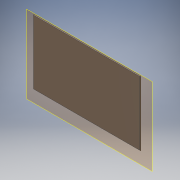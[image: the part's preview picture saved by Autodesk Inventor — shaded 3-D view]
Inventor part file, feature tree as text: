
AUTODESK INVENTOR PART (.ipt)
format: ipt  version: 2016 SP2 (Build 200236200, 236)  size: 104,448 bytes
history: native  units: mm
features: reference x12, plane x1, extrude x1, chamfer x1, sketch x1
ambient origin geometry x8: Origin, YZ Plane, XZ Plane, XY Plane, X Axis, Y Axis, Z Axis, Center Point
bodies: Body1 (feature_tree)
feature tree (16):
  plane  "Arbeitsebene1"
  extrude  "Extrusion2"  Depth=1.5mm
  chamfer  "Fase2"  Distance=0.1mm
  reference  "Referenz1"
  reference  "Referenz2"
  reference  "Referenz3"
  reference  "Referenz5"
  reference  "Referenz6"
  reference  "Referenz7"
  reference  "Referenz8"
  sketch  "Skizze2"  dims[d7=0.1mm d8=0.1mm d9=0.1mm d10=1.5mm d11=0.0mm d12=0.75mm d13=2.0mm d14=45.0deg]
  reference  "Referenz9"
  reference  "Referenz10"
  reference  "Referenz12"
  reference  "Referenz13"
  reference  "Referenz14"
